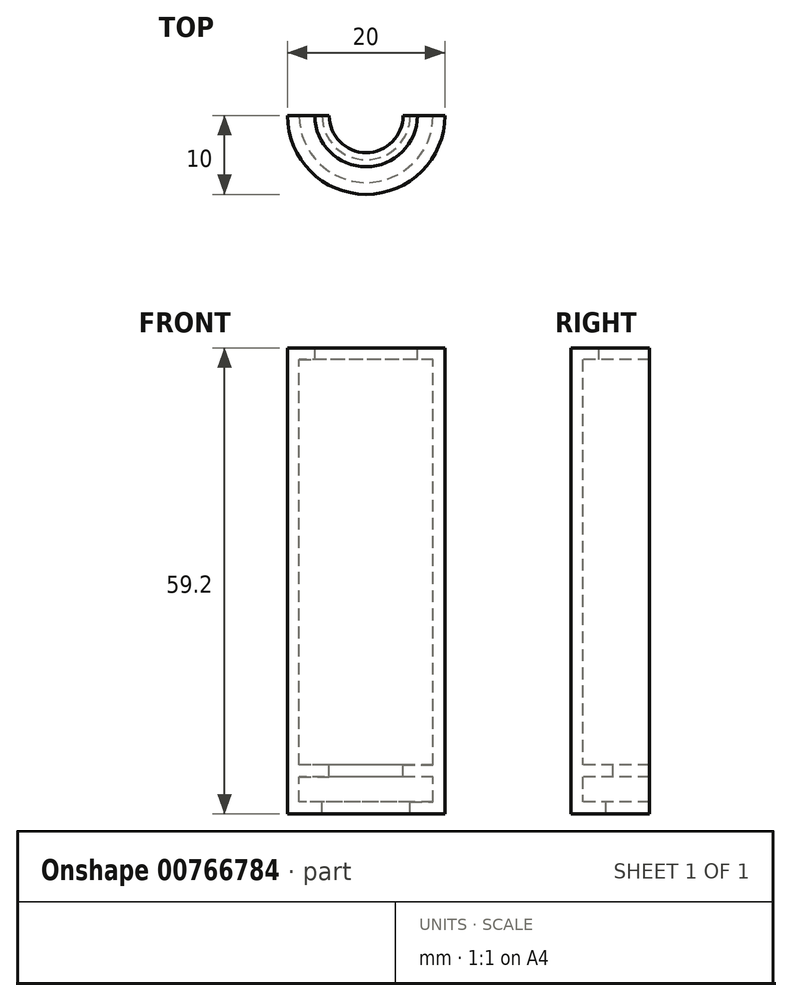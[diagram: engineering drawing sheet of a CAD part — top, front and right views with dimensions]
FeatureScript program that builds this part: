
annotation { "Feature Type Name" : "Feature", "Feature Type Description" : "" }
export const myFeature = defineFeature(function(context is Context, id is Id, definition is map)
    precondition{}
    {
        {
            var Q0;
            Q0=qCreatedBy(makeId("Front.planeOp"),FACE);
            var sketch = newSketch(context, id + "F0", { "sketchPlane" : qUnion([Q0])});
            skLineSegment(sketch, "E0", {"start": v(-6.5, 59.2) * mm, "end": v(-10, 59.2) * mm});
            skLineSegment(sketch, "E1", {"start": v(-10, 59.2) * mm, "end": v(-10, 0) * mm});
            skLineSegment(sketch, "E2", {"start": v(-10, 0) * mm, "end": v(-5.6, 0) * mm});
            skLineSegment(sketch, "E3", {"start": v(-5.6, 0) * mm, "end": v(-5.6, 1.5) * mm});
            skLineSegment(sketch, "E4", {"start": v(-5.6, 1.5) * mm, "end": v(-8.5, 1.5) * mm});
            skLineSegment(sketch, "E5", {"start": v(-8.5, 1.5) * mm, "end": v(-8.5, 4.7) * mm});
            skLineSegment(sketch, "E6", {"start": v(-8.5, 4.7) * mm, "end": v(-4.7, 4.7) * mm});
            skLineSegment(sketch, "E7", {"start": v(-4.7, 4.7) * mm, "end": v(-4.7, 6.2) * mm});
            skLineSegment(sketch, "E8", {"start": v(-4.7, 6.2) * mm, "end": v(-8.5, 6.2) * mm});
            skLineSegment(sketch, "E9", {"start": v(-8.5, 6.2) * mm, "end": v(-8.5, 57.7) * mm});
            skLineSegment(sketch, "E10", {"start": v(-8.5, 57.7) * mm, "end": v(-6.5, 57.7) * mm});
            skLineSegment(sketch, "E11", {"start": v(-6.5, 57.7) * mm, "end": v(-6.5, 59.2) * mm});
            skLineSegment(sketch, "E12", {"start": v(0, 0) * mm, "end": v(0, 59.2) * mm});
            skSolve(sketch);
        }
        {
            var Q0;
            Q0=makeQuery(id+"F0.imprint","IMPRINT",FACE,{"disambiguationData":[TD([[makeQuery(id+"F0.imprint","IMPRINT",EDGE,{"derivedFrom":sQuery(id+"F0.wireOp",EDGE,"E0")}),1.0]])]});
            var Q1;
            Q1=sQuery(id+"F0.wireOp",EDGE,"E12");
            revolve(context, id + "F1", {"surfaceOperationType" : NewSurfaceOperationType.NEW, "entities" : qUnion([Q0]), "axis" : qUnion([Q1]), "revolveType" : RevolveType.ONE_DIRECTION, "angle" : 180 * degree});
        }
    });
